# Revit family: TF-305
name_source: partatom
category: Plumbing Fixtures
revit_build: Autodesk Revit 2014 (Build: 20130308_1515(x64)
units: mm (PartAtom-declared; Revit-internal decimal feet)

## types (1)
- TF-305
    Abs Plastic = Abs Plastic
    Ac Plastic = Ac Plastic
    Available = 110-32, 110-38, 185-19, 110-WC-4.8, 185-19-0.5 and 185-19-1
    Batteries = Type "C" 4 X 1.5 V
    Brass Chromed = Brass Chromed
    Certification = http://www.helvex.com.mx
    Connection = To Convert A Manual Flush Valve Into A Sensor Flush Valve
    Description = Automatic Flushing Device Battery Powered For W.C. & Urinals With Actuating Button
    Detection Range = 19.5" - 31.5"
    Documentation = http://www.helvex.com.mx
    Features = Actuating Button
    Feeding Voltage = 6 V
    Manufacturer = Helvex
    Model = TF-305
    Power Consumption = 3 W
    Stainless Steel = Stainless Steel
    Type Comments = Flushvalves
    URL = http://www.helvex.com.mx

## geometry (parser evidence)
native form markers: Sweep x1
no freeform markers — native parametric forms only
